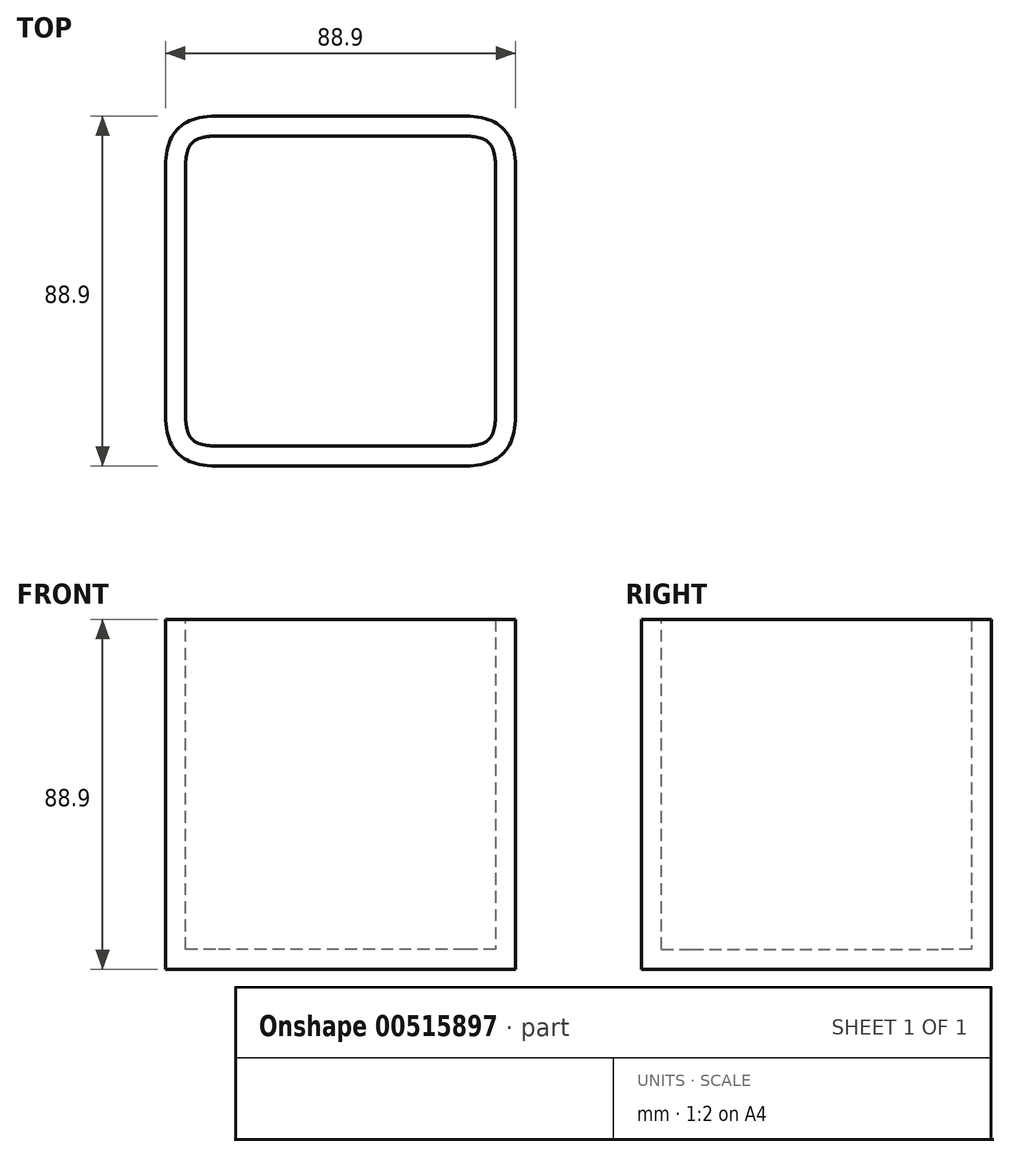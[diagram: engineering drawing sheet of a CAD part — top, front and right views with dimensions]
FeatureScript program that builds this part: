
annotation { "Feature Type Name" : "Feature", "Feature Type Description" : "" }
export const myFeature = defineFeature(function(context is Context, id is Id, definition is map)
    precondition{}
    {
        {
            var Q0;
            Q0=qCreatedBy(makeId("Top.planeOp"),FACE);
            var sketch = newSketch(context, id + "F0", { "sketchPlane" : qUnion([Q0])});
            skLineSegment(sketch, "E0.bottom", {"start": v(44.45, -44.45) * mm, "end": v(-44.45, -44.45) * mm});
            skLineSegment(sketch, "E0.top", {"start": v(44.45, 44.45) * mm, "end": v(-44.45, 44.45) * mm});
            skLineSegment(sketch, "E0.left", {"start": v(44.45, -44.45) * mm, "end": v(44.45, 44.45) * mm});
            skLineSegment(sketch, "E0.right", {"start": v(-44.45, -44.45) * mm, "end": v(-44.45, 44.45) * mm});
            skPoint(sketch, "E0.middle", {"position": v(0, 0) * mm});
            skSolve(sketch);
        }
        {
            var Q0;
            Q0=makeQuery(id+"F0.imprint","IMPRINT",FACE,{"disambiguationData":[TD([[makeQuery(id+"F0.imprint","IMPRINT",EDGE,{"derivedFrom":sQuery(id+"F0.wireOp",EDGE,"E0.bottom")}),-1.0]])]});
            extrude(context, id + "F1", {"entities" : qUnion([Q0]), "depth" : 88.9 * mm, "offsetDistance" : 25.4 * mm});
        }
        {
            var Q0;
            Q0=makeQuery(id+"F1.opExtrude","SWEPT_EDGE",EDGE,{"disambiguationData":[OSD([sQuery(id+"F0.wireOp",EDGE,"E0.bottom"),sQuery(id+"F0.wireOp",EDGE,"E0.left")])]});
            var Q1;
            Q1=makeQuery(id+"F1.opExtrude","SWEPT_EDGE",EDGE,{"disambiguationData":[OSD([sQuery(id+"F0.wireOp",EDGE,"E0.top"),sQuery(id+"F0.wireOp",EDGE,"E0.left")])]});
            var Q2;
            Q2=makeQuery(id+"F1.opExtrude","SWEPT_EDGE",EDGE,{"disambiguationData":[OSD([sQuery(id+"F0.wireOp",EDGE,"E0.bottom"),sQuery(id+"F0.wireOp",EDGE,"E0.right")])]});
            var Q3;
            Q3=makeQuery(id+"F1.opExtrude","SWEPT_EDGE",EDGE,{"disambiguationData":[OSD([sQuery(id+"F0.wireOp",EDGE,"E0.top"),sQuery(id+"F0.wireOp",EDGE,"E0.right")])]});
            fillet(context, id + "F2", {"entities" : qUnion([Q0, Q1, Q2, Q3]), "radius" : 12.7 * mm, "tangentPropagation" : true, "rho" : 0.5, "crossSection" : FilletCrossSection.CONIC, "allowEdgeOverflow" : false});
        }
        {
            var Q0;
            Q0=makeQuery(id+"F1.opExtrude","CAP_FACE",FACE,{"disambiguationData":[OSD([sQuery(id+"F0.wireOp",EDGE,"E0.bottom"),sQuery(id+"F0.wireOp",EDGE,"E0.top"),sQuery(id+"F0.wireOp",EDGE,"E0.left"),sQuery(id+"F0.wireOp",EDGE,"E0.right")])],"isStart":false});
            shell(context, id + "F3", {"entities" : qUnion([Q0]), "thickness" : 5.08 * mm});
        }
    });
